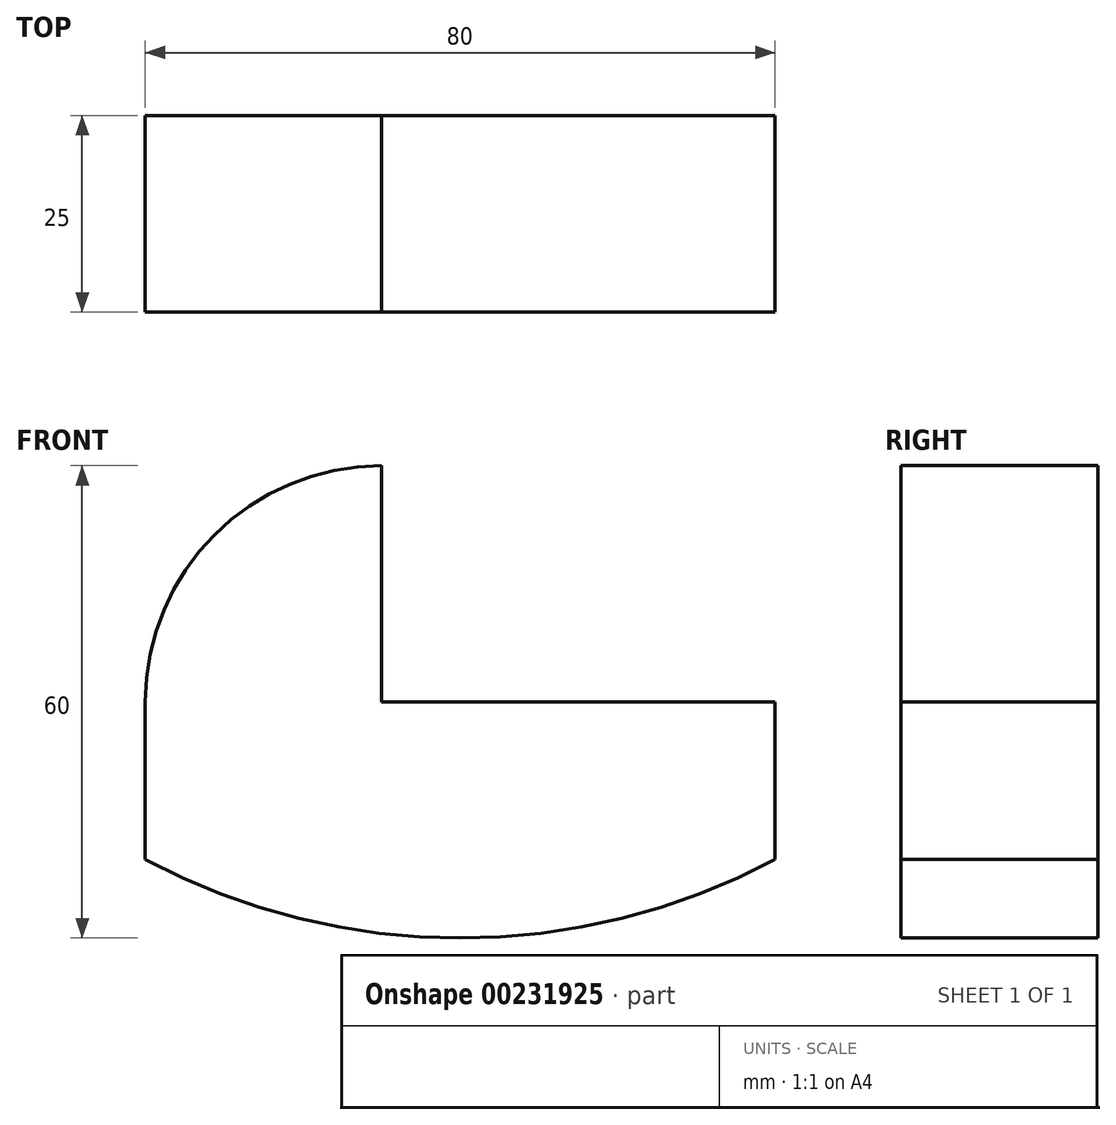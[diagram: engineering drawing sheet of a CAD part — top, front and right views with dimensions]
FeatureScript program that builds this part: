
annotation { "Feature Type Name" : "Feature", "Feature Type Description" : "" }
export const myFeature = defineFeature(function(context is Context, id is Id, definition is map)
    precondition{}
    {
        {
            var Q0;
            Q0=qCreatedBy(makeId("Front.planeOp"),FACE);
            var sketch = newSketch(context, id + "F0", { "sketchPlane" : qUnion([Q0])});
            skLineSegment(sketch, "E0", {"start": v(-50, 20) * mm, "end": v(0, 20) * mm});
            skLineSegment(sketch, "E1", {"start": v(0, 20) * mm, "end": v(0, 0) * mm});
            skArc(sketch, "E2", {"start": v(-80, 20) * mm, "mid": v(-71.21, 41.21) * mm, "end": v(-50, 50) * mm});
            skLineSegment(sketch, "E3", {"start": v(-80, 20) * mm, "end": v(-80, 0) * mm});
            skArc(sketch, "E4", {"start": v(-80, 0) * mm, "mid": v(-40, -10) * mm, "end": v(0, 0) * mm});
            skLineSegment(sketch, "E5", {"start": v(-50, 20) * mm, "end": v(-50, 50) * mm});
            skSolve(sketch);
        }
        {
            var Q0;
            Q0=makeQuery(id+"F0.imprint","IMPRINT",FACE,{"disambiguationData":[TD([[makeQuery(id+"F0.imprint","IMPRINT",EDGE,{"derivedFrom":sQuery(id+"F0.wireOp",EDGE,"E0")}),-1.0]])]});
            extrude(context, id + "F1", {"entities" : qUnion([Q0]), "depth" : 25 * mm});
        }
    });
